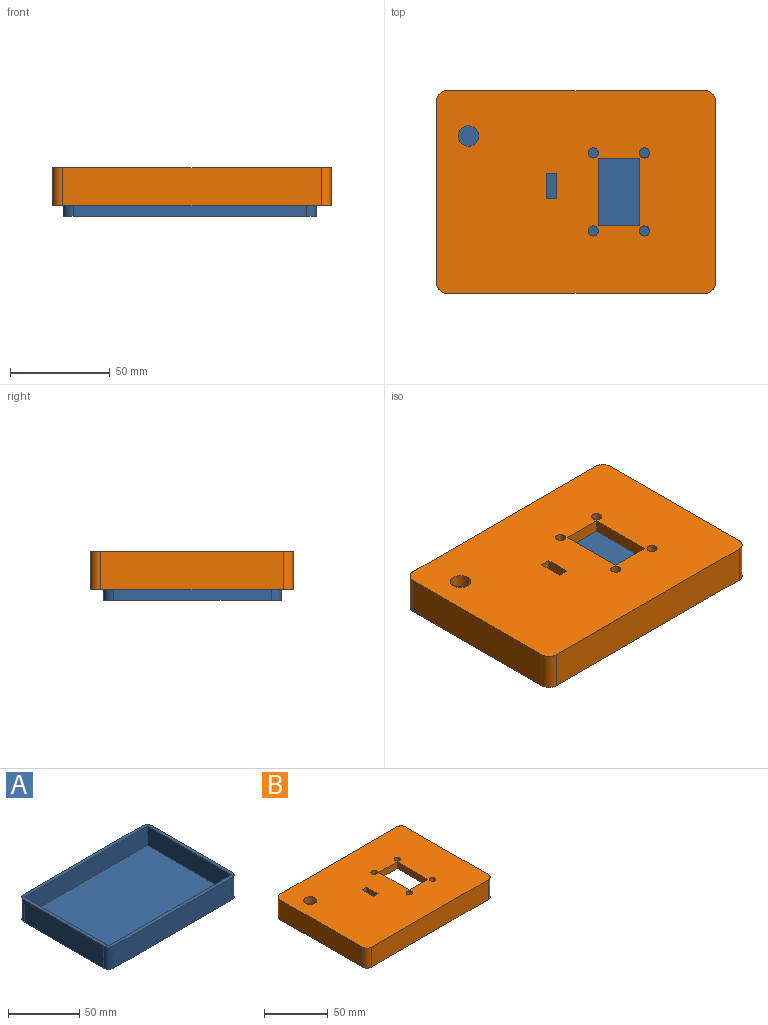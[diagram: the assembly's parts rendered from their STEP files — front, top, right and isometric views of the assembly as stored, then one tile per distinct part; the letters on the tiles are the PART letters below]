
ASSEMBLY  parts=2 mates=1
PART A: 15 faces, bbox 127x88.9x19.1 mm
  f0: plane 127x88.9mm, normal (0,0,1), area 1048.8mm2, adj f1,f2,f3,f4,f6,f7,f8,f9
  f1: plane 116.84x19.05mm, normal (0,1,0), area 2225.8mm2, adj f0,f5,f11,f14
  f2: plane 78.74x19.05mm, normal (-1,0,0), area 1500mm2, adj f0,f5,f11,f12
  f3: plane 116.84x19.05mm, normal (0,-1,0), area 2225.8mm2, adj f0,f5,f12,f13
  f4: plane 78.74x19.05mm, normal (1,0,0), area 1500mm2, adj f0,f5,f13,f14
  f5: plane 127x88.9mm, normal (0,0,-1), area 11268.1mm2, adj f1,f2,f3,f4,f11,f12,f13,f14
  f6: plane 121.92x16.51mm, normal (0,-1,0), area 2012.9mm2, adj f0,f7,f9,f10
  f7: plane 83.82x16.51mm, normal (1,0,0), area 1383.9mm2, adj f0,f6,f8,f10
  f8: plane 121.92x16.51mm, normal (0,1,0), area 2012.9mm2, adj f0,f7,f9,f10
  f9: plane 83.82x16.51mm, normal (-1,0,0), area 1383.9mm2, adj f0,f6,f8,f10
  f10: plane 121.92x83.82mm, normal (0,0,1), area 10219.3mm2, adj f6,f7,f8,f9
  f11: cylinder r=5.08mm len=19.05mm, axis (0,0,1), area 152mm2, adj f0,f1,f2,f5
  f12: cylinder r=5.08mm len=19.05mm, axis (0,0,-1), area 152mm2, adj f0,f2,f3,f5
  f13: cylinder r=5.08mm len=19.05mm, axis (0,0,1), area 152mm2, adj f0,f3,f4,f5
  f14: cylinder r=5.08mm len=19.05mm, axis (0,0,-1), area 152mm2, adj f0,f1,f4,f5
PART B: 28 faces, bbox 139.7x101.6x19.1 mm
  f0: plane 139.7x101.6mm, normal (0,0,1), area 13243.4mm2, adj f3,f4,f5,f6,f11,f12,f13,f14
  f1: plane 127x88.9mm, normal (0,0,-1), area 10362.3mm2, adj f7,f8,f9,f10,f15,f16,f17,f18
  f2: plane 139.7x101.6mm, normal (0,0,-1), area 2881.1mm2, adj f3,f4,f5,f6,f7,f8,f9,f10
  f3: plane 129.54x19.05mm, normal (0,1,0), area 2467.7mm2, adj f0,f2,f11,f14
  f4: plane 91.44x19.05mm, normal (-1,0,0), area 1741.9mm2, adj f0,f2,f11,f12
  f5: plane 129.54x19.05mm, normal (0,-1,0), area 2467.7mm2, adj f0,f2,f12,f13
  f6: plane 91.44x19.05mm, normal (1,0,0), area 1741.9mm2, adj f0,f2,f13,f14
  f7: plane 127x12.7mm, normal (0,-1,0), area 1612.9mm2, adj f1,f2,f8,f10
  f8: plane 88.9x12.7mm, normal (1,0,0), area 1129mm2, adj f1,f2,f7,f9
  f9: plane 127x12.7mm, normal (0,1,0), area 1612.9mm2, adj f1,f2,f8,f10
  f10: plane 88.9x12.7mm, normal (-1,0,0), area 1129mm2, adj f1,f2,f7,f9
  f11: cylinder r=5.08mm len=19.05mm, axis (0,0,1), area 152mm2, adj f0,f2,f3,f4
  f12: cylinder r=5.08mm len=19.05mm, axis (0,0,-1), area 152mm2, adj f0,f2,f4,f5
  f13: cylinder r=5.08mm len=19.05mm, axis (0,0,1), area 152mm2, adj f0,f2,f5,f6
  f14: cylinder r=5.08mm len=19.05mm, axis (0,0,-1), area 152mm2, adj f0,f2,f3,f6
  f15: plane 20.57x6.35mm, normal (0,-1,0), area 130.6mm2, adj f0,f1,f16,f18
  f16: plane 34.04x6.35mm, normal (1,0,0), area 216.1mm2, adj f0,f1,f15,f17
  f17: plane 20.57x6.35mm, normal (0,1,0), area 130.6mm2, adj f0,f1,f16,f18
  f18: plane 34.04x6.35mm, normal (-1,0,0), area 216.1mm2, adj f0,f1,f15,f17
  f19: cylinder r=5.11mm len=10.23mm, axis (0,0,1), area 204mm2, adj f0,f1
  f20: cylinder r=2.54mm len=6.35mm, axis (0,0,1), area 101.3mm2, adj f0,f1
  f21: cylinder r=2.54mm len=6.35mm, axis (0,0,1), area 101.3mm2, adj f0,f1
  f22: cylinder r=2.54mm len=6.35mm, axis (0,0,1), area 101.3mm2, adj f0,f1
  f23: cylinder r=2.54mm len=6.35mm, axis (0,0,1), area 101.3mm2, adj f0,f1
  f24: plane 6.35x5.08mm, normal (0,-1,0), area 32.3mm2, adj f0,f1,f25,f27
  f25: plane 12.7x6.35mm, normal (1,0,0), area 80.6mm2, adj f0,f1,f24,f26
  f26: plane 6.35x5.08mm, normal (0,1,0), area 32.3mm2, adj f0,f1,f25,f27
  f27: plane 12.7x6.35mm, normal (-1,0,0), area 80.6mm2, adj f0,f1,f24,f26
PLACE A t=(2.44,2.62,-7.72)mm fixed
PLACE B t=(3.56,2.86,-21.71)mm
MATE slider A.f10 <-> B.f1  axis (0,0,1) through (2.44,2.62,-5.18)mm
